# Revit family: Lüftungsrohrschelle , ohne AG, ohne VS, o. Gummi
name_source: partatom
category: HLS-Bauteile
revit_build: Autodesk Revit 2017 (Build: 20190507_1515(x64)
units: mm (PartAtom-declared; Revit-internal decimal feet)

## family parameters
Arbeitsebenenbasiert = Ja
Beim Laden mit Abzugskörper schneiden = Nein
Bemaßung runder Anschluss = Durchmesser verwenden
Gemeinsam genutzt = Ja
Immer vertikal = Nein
Raumberechnungspunkt = Nein
Teiletyp = Normal

## types (29) — shared parameters
Anschluss = ohne Anschluss
Bauart = zweiteilig
Fabrikat = MEFA
Firma = MEFA Befestigungs- und Montagesysteme GmbH
Material = Stahl
Materialname = S235
Mengeneinheit = St
Oberflaeche = galvanisch verzinkt
Rohraußendurchmesser Zoll = Zoll
Verschluss = Mutter / Verschluss-Schraube
Vorgabe-Ansicht = 1219 mm
max. zul. Last horizontal = 0.00 kN
max. zul. Last vertikal = 0.00 kN
vpe = 1 St
zero-valued in all types: A, DS, HGA, Stärke Material, max. Rohraußendurchmesser, min. Rohraußendurchmesser

## per-type parameters (varying)
- Lüftungsrohrschelle, o.AG, o.VS, DN  71, o.Gummi: AB=2 mm  [stored 0.00656168 ft]; Achsabstand=108 mm; Artikelnummer=0430720; B=133 mm; Breite=133 mm; D=73 mm  [stored 0.239501 ft]; DF1=25 mm  [stored 0.082021 ft]; DF2=23 mm  [stored 0.0754593 ft]; DVS=8 mm  [stored 0.0262467 ft]; EAN=4250928409379; Gewicht=0.10 kg; Gewicht pro Bauteil=0.10 kg; H=79 mm; Höhe=79 mm; Kurztext1=Lüftungsschelle Standard 20x2,0; Kurztext2=DN 71 ohne Anschluss; MB=20 mm  [stored 0.0656168 ft]; MD=2 mm  [stored 0.00656168 ft]; Materialmaße=20x2,0 mm; Nennweite DN Rohr=71 mm  [stored 0.23294 ft]; R=37 mm; RM=39 mm; Rohraußendurchmesser=73 mm  [stored 0.239501 ft]; S=108 mm; max. Höhe=79 mm; max. zul. Last=1.50 kN
- Lüftungsrohrschelle, o.AG, o.VS, DN  80, o.Gummi: AB=2 mm  [stored 0.00656168 ft]; Achsabstand=117 mm; Artikelnummer=0430810; B=142 mm; Breite=142 mm; D=82 mm  [stored 0.269029 ft]; DF1=25 mm  [stored 0.082021 ft]; DF2=23 mm  [stored 0.0754593 ft]; DVS=8 mm  [stored 0.0262467 ft]; EAN=4250928409423; Gewicht=0.11 kg; Gewicht pro Bauteil=0.11 kg; H=88 mm  [stored 0.288714 ft]; Höhe=88 mm; Kurztext1=Lüftungsschelle Standard 20x2,0; Kurztext2=DN 80 ohne Anschluss; MB=20 mm  [stored 0.0656168 ft]; MD=2 mm  [stored 0.00656168 ft]; Materialmaße=20x2,0 mm; Nennweite DN Rohr=80 mm  [stored 0.262467 ft]; R=41 mm  [stored 0.134514 ft]; RM=43 mm  [stored 0.141076 ft]; Rohraußendurchmesser=82 mm  [stored 0.269029 ft]; S=117 mm; max. Höhe=88 mm  [stored 0.288714 ft]; max. zul. Last=1.50 kN
- Lüftungsrohrschelle, o.AG, o.VS, DN  90, o.Gummi: AB=2 mm  [stored 0.00656168 ft]; Achsabstand=127 mm; Artikelnummer=0430910; B=152 mm; Breite=152 mm; D=92 mm  [stored 0.301837 ft]; DF1=25 mm  [stored 0.082021 ft]; DF2=23 mm  [stored 0.0754593 ft]; DVS=8 mm  [stored 0.0262467 ft]; EAN=4250928409478; Gewicht=0.12 kg; Gewicht pro Bauteil=0.12 kg; H=98 mm  [stored 0.321522 ft]; Höhe=98 mm; Kurztext1=Lüftungsschelle Standard 20x2,0; Kurztext2=DN 90 ohne Anschluss; MB=20 mm  [stored 0.0656168 ft]; MD=2 mm  [stored 0.00656168 ft]; Materialmaße=20x2,0 mm; Nennweite DN Rohr=90 mm  [stored 0.295276 ft]; R=46 mm  [stored 0.150919 ft]; RM=48 mm  [stored 0.15748 ft]; Rohraußendurchmesser=92 mm  [stored 0.301837 ft]; S=127 mm; max. Höhe=98 mm  [stored 0.321522 ft]; max. zul. Last=1.50 kN
- Lüftungsrohrschelle, o.AG, o.VS, DN 100, o.Gummi: AB=2 mm  [stored 0.00656168 ft]; Achsabstand=138 mm; Artikelnummer=0431010; B=163 mm; Breite=163 mm; D=103 mm; DF1=25 mm  [stored 0.082021 ft]; DF2=23 mm  [stored 0.0754593 ft]; DVS=8 mm  [stored 0.0262467 ft]; EAN=4250928409522; Gewicht=0.13 kg; Gewicht pro Bauteil=0.13 kg; H=109 mm; Höhe=109 mm; Kurztext1=Lüftungsschelle Standard 20x2,0; Kurztext2=DN 100 ohne Anschluss; MB=20 mm  [stored 0.0656168 ft]; MD=2 mm  [stored 0.00656168 ft]; Materialmaße=20x2,0 mm; Nennweite DN Rohr=100 mm; R=52 mm; RM=54 mm  [stored 0.177165 ft]; Rohraußendurchmesser=103 mm; S=138 mm; max. Höhe=109 mm; max. zul. Last=1.50 kN
- Lüftungsrohrschelle, o.AG, o.VS, DN 112, o.Gummi: AB=2 mm  [stored 0.00656168 ft]; Achsabstand=150 mm; Artikelnummer=0431130; B=175 mm; Breite=175 mm; D=115 mm; DF1=25 mm  [stored 0.082021 ft]; DF2=23 mm  [stored 0.0754593 ft]; DVS=8 mm  [stored 0.0262467 ft]; EAN=4250928409577; Gewicht=0.14 kg; Gewicht pro Bauteil=0.14 kg; H=121 mm; Höhe=121 mm; Kurztext1=Lüftungsschelle Standard 20x2,0; Kurztext2=DN 112 ohne Anschluss; MB=20 mm  [stored 0.0656168 ft]; MD=2 mm  [stored 0.00656168 ft]; Materialmaße=20x2,0 mm; Nennweite DN Rohr=112 mm; R=58 mm  [stored 0.190289 ft]; RM=60 mm; Rohraußendurchmesser=115 mm; S=150 mm; max. Höhe=121 mm; max. zul. Last=1.50 kN
- Lüftungsrohrschelle, o.AG, o.VS, DN 125, o.Gummi: AB=2 mm  [stored 0.00656168 ft]; Achsabstand=163 mm; Artikelnummer=0431260; B=188 mm; Breite=188 mm; D=128 mm; DF1=25 mm  [stored 0.082021 ft]; DF2=23 mm  [stored 0.0754593 ft]; DVS=8 mm  [stored 0.0262467 ft]; EAN=4250928409621; Gewicht=0.15 kg; Gewicht pro Bauteil=0.15 kg; H=134 mm; Höhe=134 mm; Kurztext1=Lüftungsschelle Standard 20x2,0; Kurztext2=DN 125 ohne Anschluss; MB=20 mm  [stored 0.0656168 ft]; MD=2 mm  [stored 0.00656168 ft]; Materialmaße=20x2,0 mm; Nennweite DN Rohr=125 mm; R=64 mm  [stored 0.209974 ft]; RM=66 mm  [stored 0.216535 ft]; Rohraußendurchmesser=128 mm; S=163 mm; max. Höhe=134 mm; max. zul. Last=1.50 kN
- Lüftungsrohrschelle, o.AG, o.VS, DN 140, o.Gummi: AB=2 mm  [stored 0.00656168 ft]; Achsabstand=178 mm; Artikelnummer=0431410; B=203 mm; Breite=203 mm; D=143 mm; DF1=25 mm  [stored 0.082021 ft]; DF2=23 mm  [stored 0.0754593 ft]; DVS=8 mm  [stored 0.0262467 ft]; EAN=4250928409676; Gewicht=0.17 kg; Gewicht pro Bauteil=0.17 kg; H=149 mm; Höhe=149 mm; Kurztext1=Lüftungsschelle Standard 20x2,0; Kurztext2=DN 140 ohne Anschluss; MB=20 mm  [stored 0.0656168 ft]; MD=2 mm  [stored 0.00656168 ft]; Materialmaße=20x2,0 mm; Nennweite DN Rohr=140 mm; R=72 mm; RM=74 mm; Rohraußendurchmesser=143 mm; S=178 mm; max. Höhe=149 mm; max. zul. Last=1.50 kN
- Lüftungsrohrschelle, o.AG, o.VS, DN 150, o.Gummi: AB=2 mm  [stored 0.00656168 ft]; Achsabstand=188 mm; Artikelnummer=0431510; B=213 mm; Breite=213 mm; D=153 mm; DF1=25 mm  [stored 0.082021 ft]; DF2=23 mm  [stored 0.0754593 ft]; DVS=8 mm  [stored 0.0262467 ft]; EAN=4250928409720; Gewicht=0.18 kg; Gewicht pro Bauteil=0.18 kg; H=159 mm; Höhe=159 mm; Kurztext1=Lüftungsschelle Standard 20x2,0; Kurztext2=DN 150 ohne Anschluss; MB=20 mm  [stored 0.0656168 ft]; MD=2 mm  [stored 0.00656168 ft]; Materialmaße=20x2,0 mm; Nennweite DN Rohr=150 mm; R=77 mm; RM=79 mm; Rohraußendurchmesser=153 mm; S=188 mm; max. Höhe=159 mm; max. zul. Last=1.50 kN
- Lüftungsrohrschelle, o.AG, o.VS, DN 160, o.Gummi: AB=2 mm  [stored 0.00656168 ft]; Achsabstand=198 mm; Artikelnummer=0431610; B=223 mm; Breite=223 mm; D=163 mm; DF1=25 mm  [stored 0.082021 ft]; DF2=23 mm  [stored 0.0754593 ft]; DVS=8 mm  [stored 0.0262467 ft]; EAN=4250928409775; Gewicht=0.19 kg; Gewicht pro Bauteil=0.19 kg; H=169 mm; Höhe=169 mm; Kurztext1=Lüftungsschelle Standard 20x2,0; Kurztext2=DN 160 ohne Anschluss; MB=20 mm  [stored 0.0656168 ft]; MD=2 mm  [stored 0.00656168 ft]; Materialmaße=20x2,0 mm; Nennweite DN Rohr=160 mm; R=82 mm  [stored 0.269029 ft]; RM=84 mm; Rohraußendurchmesser=163 mm; S=198 mm; max. Höhe=169 mm; max. zul. Last=1.50 kN
- Lüftungsrohrschelle, o.AG, o.VS, DN 180, o.Gummi: AB=1 mm  [stored 0.00328084 ft]; Achsabstand=218 mm; Artikelnummer=0431810; B=243 mm; Breite=243 mm; D=183 mm; DF1=25 mm  [stored 0.082021 ft]; DF2=22 mm  [stored 0.0721785 ft]; DVS=8 mm  [stored 0.0262467 ft]; EAN=4250928409829; Gewicht=0.26 kg; Gewicht pro Bauteil=0.26 kg; H=189 mm; Höhe=189 mm; Kurztext1=Lüftungsschelle Standard 20x2,5; Kurztext2=DN 180 ohne Anschluss; MB=20 mm  [stored 0.0656168 ft]; MD=3 mm  [stored 0.00984252 ft]; Materialmaße=20x2,5 mm; Nennweite DN Rohr=180 mm; R=92 mm  [stored 0.301837 ft]; RM=94 mm; Rohraußendurchmesser=183 mm; S=218 mm; max. Höhe=189 mm; max. zul. Last=2.00 kN
- Lüftungsrohrschelle, o.AG, o.VS, DN 200, o.Gummi: AB=1 mm  [stored 0.00328084 ft]; Achsabstand=238 mm; Artikelnummer=0432010; B=263 mm; Breite=263 mm; D=203 mm; DF1=25 mm  [stored 0.082021 ft]; DF2=22 mm  [stored 0.0721785 ft]; DVS=8 mm  [stored 0.0262467 ft]; EAN=4250928409874; Gewicht=0.29 kg; Gewicht pro Bauteil=0.29 kg; H=209 mm; Höhe=209 mm; Kurztext1=Lüftungsschelle Standard 20x2,5; Kurztext2=DN 200 ohne Anschluss; MB=20 mm  [stored 0.0656168 ft]; MD=3 mm  [stored 0.00984252 ft]; Materialmaße=20x2,5 mm; Nennweite DN Rohr=200 mm; R=102 mm; RM=104 mm; Rohraußendurchmesser=203 mm; S=238 mm; max. Höhe=209 mm; max. zul. Last=2.00 kN
- Lüftungsrohrschelle, o.AG, o.VS, DN 224, o.Gummi: AB=1 mm  [stored 0.00328084 ft]; Achsabstand=262 mm; Artikelnummer=0432250; B=287 mm; Breite=287 mm; D=227 mm; DF1=25 mm  [stored 0.082021 ft]; DF2=22 mm  [stored 0.0721785 ft]; DVS=8 mm  [stored 0.0262467 ft]; EAN=4250928409935; Gewicht=0.32 kg; Gewicht pro Bauteil=0.32 kg; H=233 mm; Höhe=233 mm; Kurztext1=Lüftungsschelle Standard 20x2,5; Kurztext2=DN 224 ohne Anschluss; MB=20 mm  [stored 0.0656168 ft]; MD=3 mm  [stored 0.00984252 ft]; Materialmaße=20x2,5 mm; Nennweite DN Rohr=224 mm; R=114 mm; RM=116 mm; Rohraußendurchmesser=227 mm; S=262 mm; max. Höhe=233 mm; max. zul. Last=2.00 kN
- Lüftungsrohrschelle, o.AG, o.VS, DN 250, o.Gummi: AB=1 mm  [stored 0.00328084 ft]; Achsabstand=288 mm; Artikelnummer=0432510; B=313 mm; Breite=313 mm; D=253 mm; DF1=25 mm  [stored 0.082021 ft]; DF2=22 mm  [stored 0.0721785 ft]; DVS=8 mm  [stored 0.0262467 ft]; EAN=4250928409997; Gewicht=0.35 kg; Gewicht pro Bauteil=0.35 kg; H=259 mm; Höhe=259 mm; Kurztext1=Lüftungsschelle Standard 20x2,5; Kurztext2=DN 250 ohne Anschluss; MB=20 mm  [stored 0.0656168 ft]; MD=3 mm  [stored 0.00984252 ft]; Materialmaße=20x2,5 mm; Nennweite DN Rohr=250 mm; R=127 mm; RM=129 mm; Rohraußendurchmesser=253 mm; S=288 mm; max. Höhe=259 mm; max. zul. Last=2.00 kN
- Lüftungsrohrschelle, o.AG, o.VS, DN 280, o.Gummi: AB=3 mm  [stored 0.00984252 ft]; Achsabstand=320 mm; Artikelnummer=0432810; B=346 mm; Breite=345 mm; D=283 mm; DF1=25 mm  [stored 0.082021 ft]; DF2=25 mm  [stored 0.082021 ft]; DVS=8 mm  [stored 0.0262467 ft]; EAN=4250928410054; Gewicht=0.49 kg; Gewicht pro Bauteil=0.49 kg; H=291 mm; Höhe=291 mm; Kurztext1=Lüftungsschelle Standard 25x2,5; Kurztext2=DN 280 ohne Anschluss; MB=25 mm  [stored 0.082021 ft]; MD=3 mm  [stored 0.00984252 ft]; Materialmaße=25x2,5 mm; Nennweite DN Rohr=280 mm; R=142 mm; RM=144 mm; Rohraußendurchmesser=283 mm; S=321 mm; max. Höhe=291 mm; max. zul. Last=2.00 kN
- Lüftungsrohrschelle, o.AG, o.VS, DN 300, o.Gummi: AB=4 mm  [stored 0.0131234 ft]; Achsabstand=342 mm; Artikelnummer=0433010; B=367 mm; Breite=367 mm; D=304 mm; DF1=25 mm  [stored 0.082021 ft]; DF2=25 mm  [stored 0.082021 ft]; DVS=8 mm  [stored 0.0262467 ft]; EAN=4250928410115; Gewicht=0.52 kg; Gewicht pro Bauteil=0.52 kg; H=313 mm; Höhe=313 mm; Kurztext1=Lüftungsschelle Standard 25x2,5; Kurztext2=DN 300 ohne Anschluss; MB=25 mm  [stored 0.082021 ft]; MD=3 mm  [stored 0.00984252 ft]; Materialmaße=25x2,5 mm; Nennweite DN Rohr=300 mm; R=152 mm; RM=155 mm; Rohraußendurchmesser=304 mm; S=342 mm; max. Höhe=313 mm; max. zul. Last=2.00 kN
- Lüftungsrohrschelle, o.AG, o.VS, DN 315, o.Gummi: AB=4 mm  [stored 0.0131234 ft]; Achsabstand=357 mm; Artikelnummer=0433160; B=382 mm; Breite=382 mm; D=319 mm; DF1=25 mm  [stored 0.082021 ft]; DF2=25 mm  [stored 0.082021 ft]; DVS=8 mm  [stored 0.0262467 ft]; EAN=4250928410177; Gewicht=0.54 kg; Gewicht pro Bauteil=0.54 kg; H=328 mm; Höhe=328 mm; Kurztext1=Lüftungsschelle Standard 25x2,5; Kurztext2=DN 315 ohne Anschluss; MB=25 mm  [stored 0.082021 ft]; MD=3 mm  [stored 0.00984252 ft]; Materialmaße=25x2,5 mm; Nennweite DN Rohr=315 mm; R=160 mm; RM=162 mm; Rohraußendurchmesser=319 mm; S=357 mm; max. Höhe=328 mm; max. zul. Last=2.00 kN
- Lüftungsrohrschelle, o.AG, o.VS, DN 355, o.Gummi: AB=4 mm  [stored 0.0131234 ft]; Achsabstand=397 mm; Artikelnummer=0433560; B=422 mm; Breite=422 mm; D=359 mm; DF1=25 mm  [stored 0.082021 ft]; DF2=25 mm  [stored 0.082021 ft]; DVS=8 mm  [stored 0.0262467 ft]; EAN=4250928410238; Gewicht=0.60 kg; Gewicht pro Bauteil=0.60 kg; H=368 mm; Höhe=368 mm; Kurztext1=Lüftungsschelle Standard 25x2,5; Kurztext2=DN 355 ohne Anschluss; MB=25 mm  [stored 0.082021 ft]; MD=3 mm  [stored 0.00984252 ft]; Materialmaße=25x2,5 mm; Nennweite DN Rohr=355 mm; R=180 mm; RM=182 mm; Rohraußendurchmesser=359 mm; S=397 mm; max. Höhe=368 mm; max. zul. Last=2.00 kN
- Lüftungsrohrschelle, o.AG, o.VS, DN 400, o.Gummi: AB=4 mm  [stored 0.0131234 ft]; Achsabstand=442 mm; Artikelnummer=0434010; B=467 mm; Breite=467 mm; D=404 mm; DF1=25 mm  [stored 0.082021 ft]; DF2=25 mm  [stored 0.082021 ft]; DVS=8 mm  [stored 0.0262467 ft]; EAN=4250928410290; Gewicht=0.67 kg; Gewicht pro Bauteil=0.67 kg; H=413 mm; Höhe=413 mm; Kurztext1=Lüftungsschelle Standard 25x2,5; Kurztext2=DN 400 ohne Anschluss; MB=25 mm  [stored 0.082021 ft]; MD=3 mm  [stored 0.00984252 ft]; Materialmaße=25x2,5 mm; Nennweite DN Rohr=400 mm; R=202 mm; RM=205 mm; Rohraußendurchmesser=404 mm; S=442 mm; max. Höhe=413 mm; max. zul. Last=2.00 kN
- Lüftungsrohrschelle, o.AG, o.VS, DN 450, o.Gummi: AB=4 mm  [stored 0.0131234 ft]; Achsabstand=492 mm; Artikelnummer=0434510; B=517 mm; Breite=517 mm; D=454 mm; DF1=25 mm  [stored 0.082021 ft]; DF2=25 mm  [stored 0.082021 ft]; DVS=8 mm  [stored 0.0262467 ft]; EAN=4250928410351; Gewicht=0.75 kg; Gewicht pro Bauteil=0.75 kg; H=463 mm; Höhe=463 mm; Kurztext1=Lüftungsschelle Standard 25x2,5; Kurztext2=DN 450 ohne Anschluss; MB=25 mm  [stored 0.082021 ft]; MD=3 mm  [stored 0.00984252 ft]; Materialmaße=25x2,5 mm; Nennweite DN Rohr=450 mm; R=227 mm; RM=230 mm; Rohraußendurchmesser=454 mm; S=492 mm; max. Höhe=463 mm; max. zul. Last=2.00 kN
- Lüftungsrohrschelle, o.AG, o.VS, DN 500, o.Gummi: AB=4 mm  [stored 0.0131234 ft]; Achsabstand=542 mm; Artikelnummer=0435010; B=567 mm; Breite=567 mm; D=504 mm; DF1=25 mm  [stored 0.082021 ft]; DF2=25 mm  [stored 0.082021 ft]; DVS=8 mm  [stored 0.0262467 ft]; EAN=4250928410412; Gewicht=0.83 kg; Gewicht pro Bauteil=0.83 kg; H=513 mm; Höhe=513 mm; Kurztext1=Lüftungsschelle Standard 25x2,5; Kurztext2=DN 500 ohne Anschluss; MB=25 mm  [stored 0.082021 ft]; MD=3 mm  [stored 0.00984252 ft]; Materialmaße=25x2,5 mm; Nennweite DN Rohr=500 mm; R=252 mm; RM=255 mm; Rohraußendurchmesser=504 mm; S=542 mm; max. Höhe=513 mm; max. zul. Last=2.00 kN
- Lüftungsrohrschelle, o.AG, o.VS, DN 560, o.Gummi: AB=4 mm  [stored 0.0131234 ft]; Achsabstand=602 mm; Artikelnummer=0435610; B=627 mm; Breite=627 mm; D=564 mm; DF1=25 mm  [stored 0.082021 ft]; DF2=25 mm  [stored 0.082021 ft]; DVS=8 mm  [stored 0.0262467 ft]; EAN=4250928410474; Gewicht=0.93 kg; Gewicht pro Bauteil=0.93 kg; H=573 mm; Höhe=573 mm; Kurztext1=Lüftungsschelle Standard 25x2,5; Kurztext2=DN 560 ohne Anschluss; MB=25 mm  [stored 0.082021 ft]; MD=3 mm  [stored 0.00984252 ft]; Materialmaße=25x2,5 mm; Nennweite DN Rohr=560 mm; R=282 mm; RM=285 mm; Rohraußendurchmesser=564 mm; S=602 mm; max. Höhe=573 mm; max. zul. Last=2.00 kN
- Lüftungsrohrschelle, o.AG, o.VS, DN 600, o.Gummi: AB=0 mm  [stored 0 ft]; Achsabstand=640 mm; Artikelnummer=0436010; B=665 mm; Breite=665 mm; D=605 mm; DF1=25 mm  [stored 0.082021 ft]; DF2=22 mm  [stored 0.0721785 ft]; DVS=8 mm  [stored 0.0262467 ft]; EAN=4250928410511; Gewicht=0.99 kg; Gewicht pro Bauteil=0.99 kg; H=610 mm; Höhe=610 mm; Kurztext1=Lüftungsschelle Standard 25x2,5; Kurztext2=DN 600 ohne Anschluss; MB=25 mm  [stored 0.082021 ft]; MD=3 mm  [stored 0.00984252 ft]; Materialmaße=25x2,5 mm; Nennweite DN Rohr=600 mm; R=303 mm; RM=305 mm; Rohraußendurchmesser=605 mm; S=640 mm; max. Höhe=610 mm; max. zul. Last=2.00 kN
- Lüftungsrohrschelle, o.AG, o.VS, DN 630, o.Gummi: AB=4 mm  [stored 0.0131234 ft]; Achsabstand=674 mm; Artikelnummer=0436310; B=699 mm; Breite=699 mm; D=635 mm; DF1=25 mm  [stored 0.082021 ft]; DF2=23 mm  [stored 0.0754593 ft]; DVS=10 mm  [stored 0.0328084 ft]; EAN=4250928410535; Gewicht=1.24 kg; Gewicht pro Bauteil=1.24 kg; H=645 mm; Höhe=645 mm; Kurztext1=Lüftungsschelle Standard 25x3,0; Kurztext2=DN 630 ohne Anschluss; MB=25 mm  [stored 0.082021 ft]; MD=3 mm  [stored 0.00984252 ft]; Materialmaße=25x3,0 mm; Nennweite DN Rohr=630 mm; R=318 mm; RM=321 mm; Rohraußendurchmesser=635 mm; S=674 mm; max. Höhe=645 mm; max. zul. Last=2.00 kN
- Lüftungsrohrschelle, o.AG, o.VS, DN 710, o.Gummi: AB=4 mm  [stored 0.0131234 ft]; Achsabstand=754 mm; Artikelnummer=0437110; B=779 mm; Breite=779 mm; D=715 mm; DF1=25 mm  [stored 0.082021 ft]; DF2=23 mm  [stored 0.0754593 ft]; DVS=10 mm  [stored 0.0328084 ft]; EAN=4250928410559; Gewicht=1.40 kg; Gewicht pro Bauteil=1.40 kg; H=725 mm; Höhe=725 mm; Kurztext1=Lüftungsschelle Standard 25x3,0; Kurztext2=DN 710 ohne Anschluss; MB=25 mm  [stored 0.082021 ft]; MD=3 mm  [stored 0.00984252 ft]; Materialmaße=25x3,0 mm; Nennweite DN Rohr=710 mm; R=358 mm; RM=361 mm; Rohraußendurchmesser=715 mm; S=754 mm; max. Höhe=725 mm; max. zul. Last=2.00 kN
- Lüftungsrohrschelle, o.AG, o.VS, DN 800, o.Gummi: AB=5 mm  [stored 0.0164042 ft]; Achsabstand=845 mm; Artikelnummer=0438010; B=869 mm; Breite=870 mm; D=805 mm; DF1=25 mm  [stored 0.082021 ft]; DF2=23 mm  [stored 0.0754593 ft]; DVS=10 mm  [stored 0.0328084 ft]; EAN=4250928410573; Gewicht=1.56 kg; Gewicht pro Bauteil=1.56 kg; H=816 mm; Höhe=816 mm; Kurztext1=Lüftungsschelle Standard 25x3,0; Kurztext2=DN 800 ohne Anschluss; MB=25 mm  [stored 0.082021 ft]; MD=3 mm  [stored 0.00984252 ft]; Materialmaße=25x3,0 mm; Nennweite DN Rohr=800 mm; R=403 mm; RM=406 mm; Rohraußendurchmesser=805 mm; S=844 mm; max. Höhe=816 mm; max. zul. Last=2.00 kN
- Lüftungsrohrschelle, o.AG, o.VS, DN 900, o.Gummi: AB=5 mm  [stored 0.0164042 ft]; Achsabstand=945 mm; Artikelnummer=0439010; B=971 mm; Breite=970 mm; D=905 mm; DF1=25 mm  [stored 0.082021 ft]; DF2=25 mm  [stored 0.082021 ft]; DVS=10 mm  [stored 0.0328084 ft]; EAN=4250928410597; Gewicht=2.10 kg; Gewicht pro Bauteil=2.10 kg; H=916 mm; Höhe=916 mm; Kurztext1=Lüftungsschelle Standard 30x3,0; Kurztext2=DN 900 ohne Anschluss; MB=30 mm  [stored 0.0984252 ft]; MD=3 mm  [stored 0.00984252 ft]; Materialmaße=30x3,0 mm; Nennweite DN Rohr=900 mm; R=453 mm; RM=456 mm; Rohraußendurchmesser=905 mm; S=946 mm; max. Höhe=916 mm; max. zul. Last=2.00 kN
- Lüftungsrohrschelle, o.AG, o.VS, DN1000, o.Gummi: AB=6 mm  [stored 0.019685 ft]; Achsabstand=1047 mm; Artikelnummer=0440010; B=1072 mm; Breite=1 mm  [stored 0.00328084 ft]; D=1006 mm; DF1=25 mm  [stored 0.082021 ft]; DF2=25 mm  [stored 0.082021 ft]; DVS=10 mm  [stored 0.0328084 ft]; EAN=4250928410610; Gewicht=2.34 kg; Gewicht pro Bauteil=2.34 kg; H=1018 mm; Höhe=1018 mm; Kurztext1=Lüftungsschelle Standard 30x3,0; Kurztext2=DN 1000 ohne Anschluss; MB=30 mm  [stored 0.0984252 ft]; MD=3 mm  [stored 0.00984252 ft]; Materialmaße=30x3,0 mm; Nennweite DN Rohr=1 mm  [stored 0.00328084 ft]; R=503 mm; RM=506 mm; Rohraußendurchmesser=1006 mm; S=1047 mm; max. Höhe=1 mm  [stored 0.00328084 ft]; max. zul. Last=2.00 kN
- Lüftungsrohrschelle, o.AG, o.VS, DN1120, o.Gummi: AB=6 mm  [stored 0.019685 ft]; Achsabstand=1167 mm; Artikelnummer=0441210; B=1192 mm; Breite=1 mm  [stored 0.00328084 ft]; D=1126 mm; DF1=25 mm  [stored 0.082021 ft]; DF2=25 mm  [stored 0.082021 ft]; DVS=10 mm  [stored 0.0328084 ft]; EAN=4250928410634; Gewicht=2.62 kg; Gewicht pro Bauteil=2.62 kg; H=1138 mm; Höhe=1138 mm; Kurztext1=Lüftungsschelle Standard 30x3,0; Kurztext2=DN 1120 ohne Anschluss; MB=30 mm  [stored 0.0984252 ft]; MD=3 mm  [stored 0.00984252 ft]; Materialmaße=30x3,0 mm; Nennweite DN Rohr=1 mm  [stored 0.00328084 ft]; R=563 mm; RM=566 mm; Rohraußendurchmesser=1126 mm; S=1167 mm; max. Höhe=1 mm  [stored 0.00328084 ft]; max. zul. Last=2.00 kN
- Lüftungsrohrschelle, o.AG, o.VS, DN1250, o.Gummi: AB=6 mm  [stored 0.019685 ft]; Achsabstand=1297 mm; Artikelnummer=0442510; B=1327 mm; Breite=1 mm  [stored 0.00328084 ft]; D=1256 mm; DF1=30 mm  [stored 0.0984252 ft]; DF2=25 mm  [stored 0.082021 ft]; DVS=10 mm  [stored 0.0328084 ft]; EAN=4250928410658; Gewicht=2.91 kg; Gewicht pro Bauteil=2.91 kg; H=1268 mm; Höhe=1268 mm; Kurztext1=Lüftungsschelle Standard 30x3,0; Kurztext2=DN 1250 ohne Anschluss; MB=30 mm  [stored 0.0984252 ft]; MD=3 mm  [stored 0.00984252 ft]; Materialmaße=30x3,0 mm; Nennweite DN Rohr=1 mm  [stored 0.00328084 ft]; R=628 mm; RM=631 mm; Rohraußendurchmesser=1256 mm; S=1297 mm; max. Höhe=1 mm  [stored 0.00328084 ft]; max. zul. Last=2.00 kN

note: [stored X ft] marks values corroborated as IEEE doubles in the binary element streams (Revit-internal decimal feet)

## geometry (parser evidence)
native form markers: Sweep x7
no freeform markers — native parametric forms only
